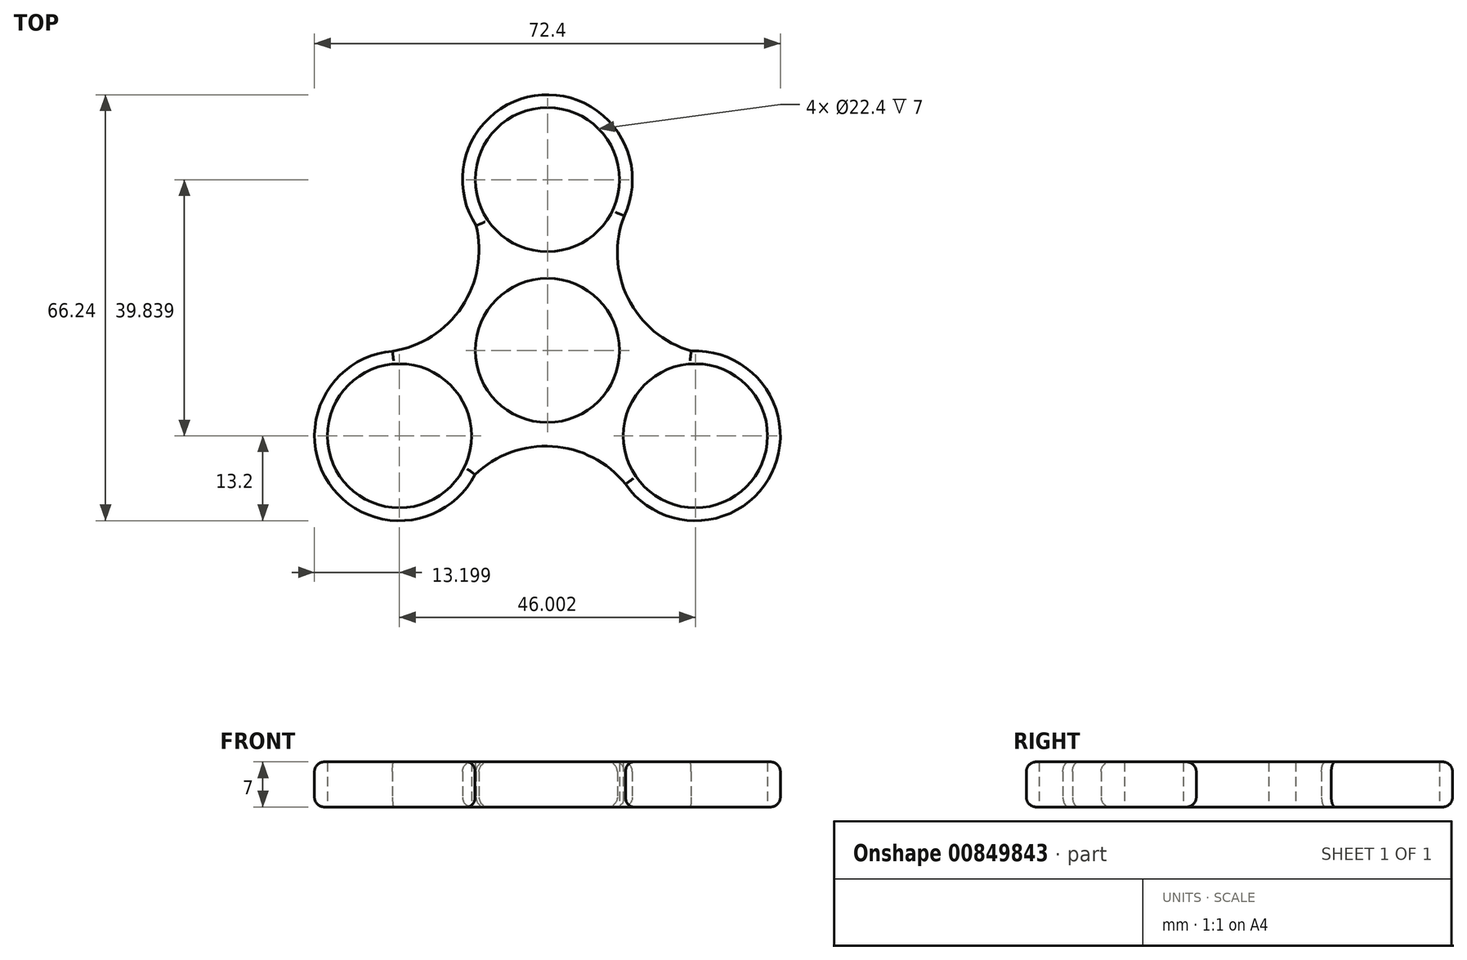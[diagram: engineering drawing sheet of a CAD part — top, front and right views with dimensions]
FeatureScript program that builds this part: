
annotation { "Feature Type Name" : "Feature", "Feature Type Description" : "" }
export const myFeature = defineFeature(function(context is Context, id is Id, definition is map)
    precondition{}
    {
        {
            var Q0;
            Q0=qCreatedBy(makeId("Top.planeOp"),FACE);
            var sketch = newSketch(context, id + "F0", { "sketchPlane" : qUnion([Q0])});
            skCircle(sketch, "E0", {"center": v(0, 0) * mm, "radius": 11.2 * mm});
            skCircle(sketch, "E1", {"center": v(0, 26.56) * mm, "radius": 11.2 * mm});
            skArc(sketch, "E2", {"start": v(11.93, 20.92) * mm, "mid": v(-0.87, 39.73) * mm, "end": v(-11.09, 19.4) * mm});
            skArc(sketch, "E3.1.0", {"start": v(-24.08, -0.12) * mm, "mid": v(-33.97, -20.62) * mm, "end": v(-11.25, -19.3) * mm});
            skCircle(sketch, "E3.1.1", {"center": v(-23, -13.28) * mm, "radius": 11.2 * mm});
            skArc(sketch, "E3.2.0", {"start": v(12.15, -20.8) * mm, "mid": v(34.84, -19.11) * mm, "end": v(22.34, -0.1) * mm});
            skCircle(sketch, "E3.2.1", {"center": v(23, -13.28) * mm, "radius": 11.2 * mm});
            skArc(sketch, "E4", {"start": v(11.93, 20.92) * mm, "mid": v(12.52, 8.13) * mm, "end": v(22.34, -0.1) * mm});
            skArc(sketch, "E5.1.0", {"start": v(-24.08, -0.12) * mm, "mid": v(-13.3, 6.78) * mm, "end": v(-11.09, 19.4) * mm});
            skArc(sketch, "E5.2.0", {"start": v(12.15, -20.8) * mm, "mid": v(0.78, -14.9) * mm, "end": v(-11.25, -19.3) * mm});
            skSolve(sketch);
        }
        {
            var Q0;
            Q0=makeQuery(id+"F0.imprint","IMPRINT",FACE,{"disambiguationData":[TD([[makeQuery(id+"F0.imprint","IMPRINT",EDGE,{"derivedFrom":sQuery(id+"F0.wireOp",EDGE,"E0")}),-1.0]])]});
            extrude(context, id + "F1", {"entities" : qUnion([Q0]), "depth" : 7 * mm, "offsetDistance" : 25 * mm});
        }
        {
            var Q0;
            Q0=makeQuery(id+"F1.opExtrude","CAP_EDGE",EDGE,{"disambiguationData":[OSD([sQuery(id+"F0.wireOp",EDGE,"E5.2.0")])],"isStart":false});
            var Q1;
            Q1=makeQuery(id+"F1.opExtrude","CAP_EDGE",EDGE,{"disambiguationData":[OSD([sQuery(id+"F0.wireOp",EDGE,"E5.2.0")])],"isStart":true});
            var Q2;
            Q2=makeQuery(id+"F1.opExtrude","CAP_EDGE",EDGE,{"disambiguationData":[OSD([sQuery(id+"F0.wireOp",EDGE,"E3.1.0")])],"isStart":false});
            var Q3;
            Q3=makeQuery(id+"F1.opExtrude","CAP_EDGE",EDGE,{"disambiguationData":[OSD([sQuery(id+"F0.wireOp",EDGE,"E5.1.0")])],"isStart":false});
            var Q4;
            Q4=makeQuery(id+"F1.opExtrude","CAP_EDGE",EDGE,{"disambiguationData":[OSD([sQuery(id+"F0.wireOp",EDGE,"E2")])],"isStart":false});
            var Q5;
            Q5=makeQuery(id+"F1.opExtrude","CAP_EDGE",EDGE,{"disambiguationData":[OSD([sQuery(id+"F0.wireOp",EDGE,"E4")])],"isStart":false});
            var Q6;
            Q6=makeQuery(id+"F1.opExtrude","CAP_EDGE",EDGE,{"disambiguationData":[OSD([sQuery(id+"F0.wireOp",EDGE,"E3.2.0")])],"isStart":false});
            fillet(context, id + "F2", {"entities" : qUnion([Q0, Q1, Q2, Q3, Q4, Q5, Q6]), "radius" : 1.5 * mm, "tangentPropagation" : true, "allowEdgeOverflow" : false});
        }
        {
            var Q0;
            Q0=makeQuery(id+"F1.opExtrude","CAP_EDGE",EDGE,{"disambiguationData":[OSD([sQuery(id+"F0.wireOp",EDGE,"E3.1.0")])],"isStart":true});
            var Q1;
            {var subQ0=sQuery(id+"F0.wireOp",EDGE,"E5.2.0");Q1=makeQuery(id+"F2.opFillet","BLEND_EDGE",EDGE,{"blendedFrom":[makeQuery(id+"F1.opExtrude","CAP_EDGE",EDGE,{"disambiguationData":[OSD([subQ0])],"isStart":true}),makeQuery(id+"F1.opExtrude","CAP_FACE",FACE,{"disambiguationData":[OSD([sQuery(id+"F0.wireOp",EDGE,"E0"),sQuery(id+"F0.wireOp",EDGE,"E1"),sQuery(id+"F0.wireOp",EDGE,"E2"),sQuery(id+"F0.wireOp",EDGE,"E3.1.0"),sQuery(id+"F0.wireOp",EDGE,"E3.1.1"),sQuery(id+"F0.wireOp",EDGE,"E3.2.0"),sQuery(id+"F0.wireOp",EDGE,"E3.2.1"),sQuery(id+"F0.wireOp",EDGE,"E4"),sQuery(id+"F0.wireOp",EDGE,"E5.1.0"),subQ0])],"isStart":true})],"blendedInto":[makeQuery(id+"F1.opExtrude","CAP_FACE",FACE,{"disambiguationData":[OSD([sQuery(id+"F0.wireOp",EDGE,"E0"),sQuery(id+"F0.wireOp",EDGE,"E1"),sQuery(id+"F0.wireOp",EDGE,"E2"),sQuery(id+"F0.wireOp",EDGE,"E3.1.0"),sQuery(id+"F0.wireOp",EDGE,"E3.1.1"),sQuery(id+"F0.wireOp",EDGE,"E3.2.0"),sQuery(id+"F0.wireOp",EDGE,"E3.2.1"),sQuery(id+"F0.wireOp",EDGE,"E4"),sQuery(id+"F0.wireOp",EDGE,"E5.1.0"),subQ0])],"isStart":true})]});}
            var Q2;
            Q2=makeQuery(id+"F1.opExtrude","CAP_EDGE",EDGE,{"disambiguationData":[OSD([sQuery(id+"F0.wireOp",EDGE,"E3.2.0")])],"isStart":true});
            var Q3;
            Q3=makeQuery(id+"F1.opExtrude","CAP_EDGE",EDGE,{"disambiguationData":[OSD([sQuery(id+"F0.wireOp",EDGE,"E4")])],"isStart":true});
            var Q4;
            Q4=makeQuery(id+"F1.opExtrude","CAP_EDGE",EDGE,{"disambiguationData":[OSD([sQuery(id+"F0.wireOp",EDGE,"E2")])],"isStart":true});
            var Q5;
            Q5=makeQuery(id+"F1.opExtrude","CAP_EDGE",EDGE,{"disambiguationData":[OSD([sQuery(id+"F0.wireOp",EDGE,"E5.1.0")])],"isStart":true});
            fillet(context, id + "F3", {"entities" : qUnion([Q0, Q1, Q2, Q3, Q4, Q5]), "radius" : 1.5 * mm, "tangentPropagation" : true, "allowEdgeOverflow" : false});
        }
    });
